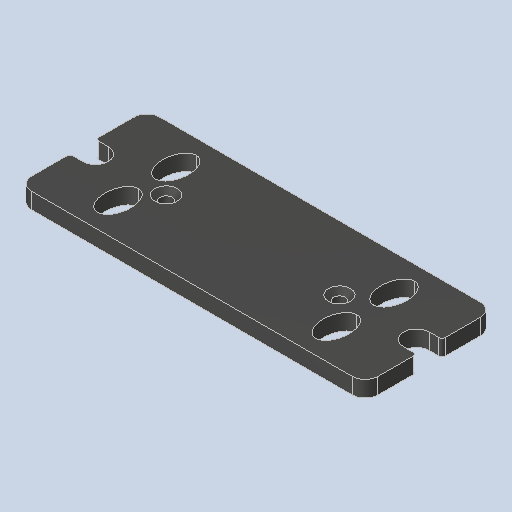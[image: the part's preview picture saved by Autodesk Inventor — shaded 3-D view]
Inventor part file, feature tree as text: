
AUTODESK INVENTOR PART (.ipt)
format: ipt  version: 2023.4 (Build 274418000, 418)  size: 124,416 bytes
history: native  units: in
note: dims shown in document units (in); Inventor stores cm internally (conversion verified against a paired STEP export)
features: mirror x1
ambient origin geometry x8: Origin, YZ Plane, XZ Plane, XY Plane, X Axis, Y Axis, Z Axis, Center Point
bodies: Solid1 (feature_tree)
feature tree (1):
  mirror  "Mirror2"
